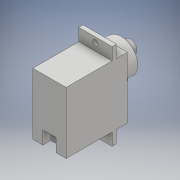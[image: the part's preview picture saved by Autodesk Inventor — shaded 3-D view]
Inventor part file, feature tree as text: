
AUTODESK INVENTOR PART (.ipt)
format: ipt  version: 2018 (Build 220112000, 112)  size: 195,072 bytes
history: native  units: mm
features: extrude x7, sketch x7, other x3
ambient origin geometry x8: Origin, YZ Plane, XZ Plane, XY Plane, X Axis, Y Axis, Z Axis, Center Point
bodies: Body1 (feature_tree)
feature tree (17):
  other  "Sólido1"
  extrude  "Extrusión1"  Depth=23.2mm
  extrude  "Extrusión2"  Depth=17.3mm
  other  "Edición directa1"
  extrude  "Extrusión3"  Depth=1.6mm
  extrude  "Extrusión4"  Depth=11.8mm TaperAngle=0.0deg
  extrude  "Extrusión5"  Depth=0.7mm
  extrude  "Extrusión6"  Depth=2.0mm
  extrude  "Extrusión7"  Depth=2.4mm TaperAngle=0.0deg
  sketch  "Boceto1"  dims[d0=11.8mm d1=23.2mm]
  sketch  "Boceto2"  dims[d2=23.0mm d3=0.0mm d4=17.3mm]
  sketch  "Boceto4"  dims[d5=4.7mm d6=1.6mm]
  sketch  "Boceto5"  dims[d7=4.7mm d8=11.8mm d9=0.0mm]
  sketch  "Boceto6"  dims[d10=0.0mm d11=0.0mm d12=0.7mm d13=1.9mm]
  sketch  "Boceto7"  dims[d14=1.9mm d15=2.0mm]
  sketch  "Boceto8"  dims[d16=2.0mm d17=2.4mm d18=0.0mm d19=15.0mm d20=4.0mm d21=0.0mm d22=5.0mm d23=4.8mm d24=3.5mm d25=0.0mm d26=6.25mm d28=4.3mm d29=0.0mm d30=3.0mm d31=2.5mm d32=2.5mm d33=5.0mm d34=0.0mm d35=4.1mm d36=23.0mm]
  other  "Desplazar1"
